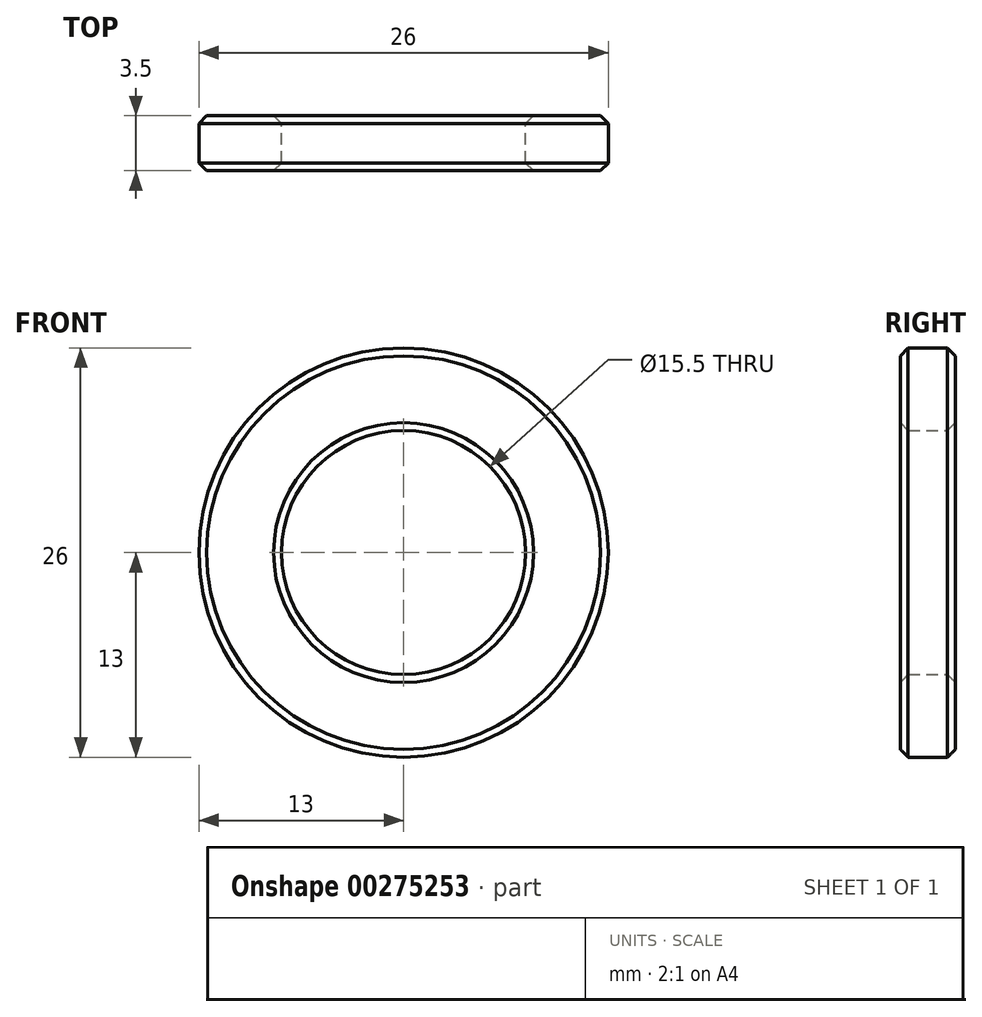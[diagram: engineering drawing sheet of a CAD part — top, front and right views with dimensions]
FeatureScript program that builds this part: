
annotation { "Feature Type Name" : "Feature", "Feature Type Description" : "" }
export const myFeature = defineFeature(function(context is Context, id is Id, definition is map)
    precondition{}
    {
        {
            var Q0;
            Q0=qCreatedBy(makeId("Front.planeOp"),FACE);
            var sketch = newSketch(context, id + "F0", { "sketchPlane" : qUnion([Q0])});
            skCircle(sketch, "E0", {"center": v(0, 0) * mm, "radius": 13 * mm});
            skCircle(sketch, "E1", {"center": v(0, 0) * mm, "radius": 7.75 * mm});
            skSolve(sketch);
        }
        {
            var Q0;
            Q0=makeQuery(id+"F0.imprint","IMPRINT",FACE,{"disambiguationData":[TD([[makeQuery(id+"F0.imprint","IMPRINT",EDGE,{"derivedFrom":sQuery(id+"F0.wireOp",EDGE,"E0")}),1.0]])]});
            extrude(context, id + "F1", {"entities" : qUnion([Q0]), "depth" : 3.5 * mm});
        }
        {
            var Q0;
            Q0=makeQuery(id+"F1.opExtrude","CAP_EDGE",EDGE,{"disambiguationData":[OSD([sQuery(id+"F0.wireOp",EDGE,"E0")])],"isStart":false});
            var Q1;
            Q1=makeQuery(id+"F1.opExtrude","CAP_EDGE",EDGE,{"disambiguationData":[OSD([sQuery(id+"F0.wireOp",EDGE,"E0")])],"isStart":true});
            chamfer(context, id + "F2", {"entities" : qUnion([Q0, Q1]), "chamferType" : ChamferType.OFFSET_ANGLE, "width" : .5 * mm, "oppositeDirection" : false, "angle" : 45 * degree, "tangentPropagation" : true});
        }
        {
            var Q0;
            Q0=makeQuery(id+"F1.opExtrude","CAP_EDGE",EDGE,{"disambiguationData":[OSD([sQuery(id+"F0.wireOp",EDGE,"E1")])],"isStart":true});
            var Q1;
            Q1=makeQuery(id+"F1.opExtrude","CAP_EDGE",EDGE,{"disambiguationData":[OSD([sQuery(id+"F0.wireOp",EDGE,"E1")])],"isStart":false});
            chamfer(context, id + "F3", {"entities" : qUnion([Q0, Q1]), "width" : .5 * mm, "tangentPropagation" : true});
        }
    });
